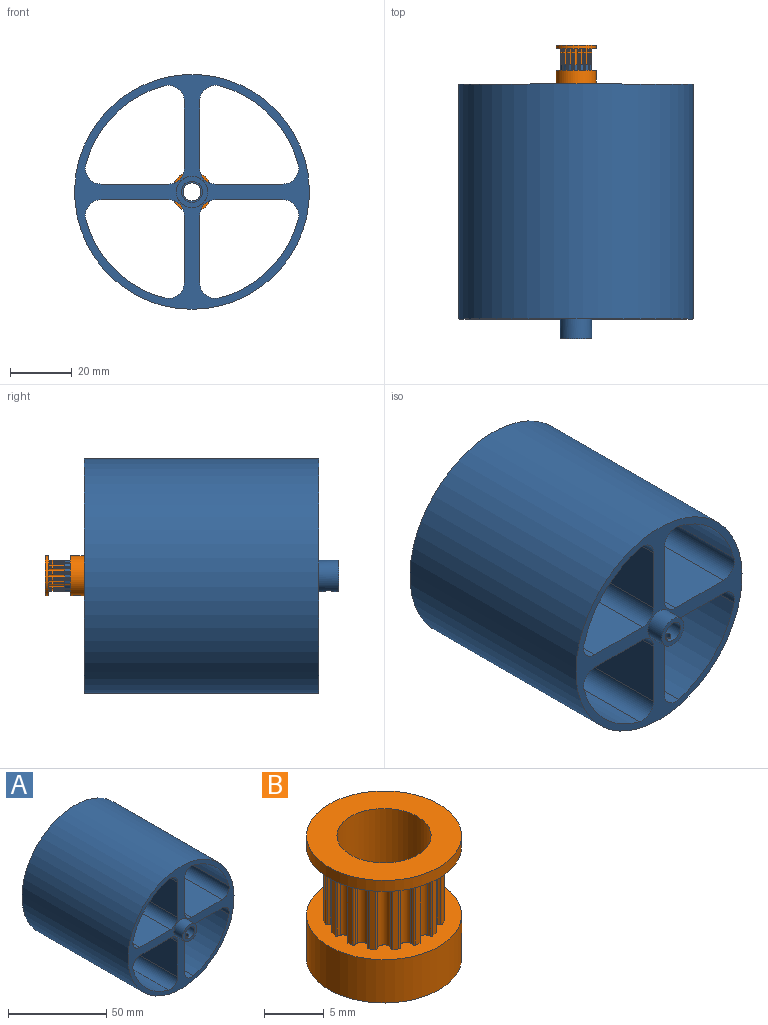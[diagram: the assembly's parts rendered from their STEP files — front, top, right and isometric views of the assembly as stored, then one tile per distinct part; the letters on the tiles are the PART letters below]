
ASSEMBLY  parts=2 mates=1
PART A: 38 faces, bbox 76.2x88.9x76.2 mm
  f0: plane 6.86x6.86mm, normal (0,-1,0), area 10.1mm2, adj f2,f33
  f1: plane 6.86x6.86mm, normal (0,1,0), area 10.1mm2, adj f2,f3
  f2: cylinder r=2.92mm len=76.2mm, axis (0,1,0), area 1398.5mm2, adj f0,f1
  f3: cylinder r=3.43mm len=6.86mm, axis (0,-1,0), area 128.7mm2, adj f1,f4,f37
  f4: plane 10.16x10.16mm, normal (0,1,0), area 44.1mm2, adj f3,f5
  f5: cylinder r=5.08mm len=10.16mm, axis (0,-1,0), area 194.7mm2, adj f4,f32,f37
  f6: cylinder r=5.08mm len=76.2mm, axis (0,1,0), area 705.9mm2, adj f7,f11,f30,f32
  f7: plane 76.2x21.89mm, normal (-1,0,0), area 1668.2mm2, adj f6,f8,f30,f32
  f8: cylinder r=5.08mm len=76.2mm, axis (0,-1,0), area 608mm2, adj f7,f9,f30,f32
  f9: plane 76.2x21.89mm, normal (0,0,1), area 1668.2mm2, adj f8,f10,f30,f32
  f10: cylinder r=5.08mm len=76.2mm, axis (0,1,0), area 705.9mm2, adj f9,f11,f30,f32
  f11: cylinder r=35.56mm len=76.2mm, axis (0,1,0), area 2887mm2, adj f6,f10,f30,f32
  f12: cylinder r=5.08mm len=76.2mm, axis (0,1,0), area 705.9mm2, adj f13,f17,f30,f32
  f13: plane 76.2x21.89mm, normal (1,0,0), area 1668.2mm2, adj f12,f14,f30,f32
  f14: cylinder r=5.08mm len=76.2mm, axis (0,-1,0), area 608mm2, adj f13,f15,f30,f32
  f15: plane 76.2x21.89mm, normal (0,0,-1), area 1668.2mm2, adj f14,f16,f30,f32
  f16: cylinder r=5.08mm len=76.2mm, axis (0,1,0), area 705.9mm2, adj f15,f17,f30,f32
  f17: cylinder r=35.56mm len=76.2mm, axis (0,1,0), area 2887mm2, adj f12,f16,f30,f32
  f18: cylinder r=38.1mm len=76.2mm, axis (0,1,0), area 18241.5mm2, adj f30,f32
  f19: cylinder r=5.08mm len=76.2mm, axis (0,1,0), area 705.9mm2, adj f20,f24,f30,f32
  f20: cylinder r=35.56mm len=76.2mm, axis (0,1,0), area 2887mm2, adj f19,f21,f30,f32
  f21: cylinder r=5.08mm len=76.2mm, axis (0,1,0), area 705.9mm2, adj f20,f22,f30,f32
  f22: plane 76.2x21.89mm, normal (0,0,-1), area 1668.2mm2, adj f21,f23,f30,f32
  f23: cylinder r=5.08mm len=76.2mm, axis (0,-1,0), area 608mm2, adj f22,f24,f30,f32
  f24: plane 76.2x21.89mm, normal (-1,0,0), area 1668.2mm2, adj f19,f23,f30,f32
  f25: cylinder r=5.08mm len=76.2mm, axis (0,1,0), area 705.9mm2, adj f26,f30,f31,f32
  f26: plane 76.2x21.89mm, normal (0,0,1), area 1668.2mm2, adj f25,f27,f30,f32
  f27: cylinder r=5.08mm len=76.2mm, axis (0,-1,0), area 608mm2, adj f26,f28,f30,f32
  f28: plane 76.2x21.89mm, normal (1,0,0), area 1668.2mm2, adj f27,f29,f30,f32
  f29: cylinder r=5.08mm len=76.2mm, axis (0,1,0), area 705.9mm2, adj f28,f30,f31,f32
  f30: plane 76.2x76.2mm, normal (0,-1,0), area 1293.1mm2, adj f6,f7,f8,f9,f10,f11,f12,f13
  f31: cylinder r=35.56mm len=76.2mm, axis (0,1,0), area 2887mm2, adj f25,f29,f30,f32
  f32: plane 76.2x76.2mm, normal (0,1,0), area 1293.1mm2, adj f5,f6,f7,f8,f9,f10,f11,f12
  f33: cylinder r=3.43mm len=6.86mm, axis (0,-1,0), area 128.7mm2, adj f0,f35,f36
  f34: cylinder r=5.08mm len=10.16mm, axis (0,-1,0), area 194.7mm2, adj f30,f35,f36
  f35: plane 10.16x10.16mm, normal (0,-1,0), area 44.1mm2, adj f33,f34
  f36: cylinder r=1.59mm len=3.18mm, axis (0,0,1), area 17.1mm2, adj f33,f34
  f37: cylinder r=1.59mm len=3.18mm, axis (0,0,1), area 17.1mm2, adj f3,f5
PART B: 104 faces, bbox 13x13x12.6 mm
  f0: cylinder r=3.94mm len=12.58mm, axis (0,0,1), area 304.5mm2, adj f2,f102,f103
  f1: cylinder r=6.5mm len=13mm, axis (0,0,1), area 174.4mm2, adj f2,f3,f103
  f2: plane 13x13mm, normal (0,0,-1), area 83.8mm2, adj f0,f1
  f3: plane 13x13mm, normal (0,0,1), area 62.7mm2, adj f1,f4,f5,f6,f7,f8,f9,f10
  f4: cylinder r=0.15mm len=7mm, axis (0,0,-1), area 1.7mm2, adj f3,f5,f99,f100
  f5: cylinder r=1mm len=7mm, axis (0,0,-1), area 1.7mm2, adj f3,f4,f6,f100
  f6: cylinder r=0.56mm len=7mm, axis (0,0,-1), area 9mm2, adj f3,f5,f7,f100
  f7: cylinder r=1mm len=7mm, axis (0,0,-1), area 1.7mm2, adj f3,f6,f8,f100
  f8: cylinder r=0.15mm len=7mm, axis (0,0,-1), area 1.7mm2, adj f3,f7,f9,f100
  f9: plane 7x0.49mm, normal (0.98,0.2,0), area 3.5mm2, adj f3,f8,f10,f100
  f10: cylinder r=0.15mm len=7mm, axis (0,0,-1), area 1.7mm2, adj f3,f9,f11,f100
  f11: cylinder r=1mm len=7mm, axis (0,0,-1), area 1.7mm2, adj f3,f10,f12,f100
  f12: cylinder r=0.56mm len=7mm, axis (0,0,-1), area 9mm2, adj f3,f11,f13,f100
  f13: cylinder r=1mm len=7mm, axis (0,0,-1), area 1.7mm2, adj f3,f12,f14,f100
  f14: cylinder r=0.15mm len=7mm, axis (0,0,-1), area 1.7mm2, adj f3,f13,f15,f100
  f15: plane 7x0.41mm, normal (0.83,0.56,0), area 3.5mm2, adj f3,f14,f16,f100
  f16: cylinder r=0.15mm len=7mm, axis (0,0,-1), area 1.7mm2, adj f3,f15,f17,f100
  f17: cylinder r=1mm len=7mm, axis (0,0,-1), area 1.7mm2, adj f3,f16,f18,f100
  f18: cylinder r=0.56mm len=7mm, axis (0,0,-1), area 9mm2, adj f3,f17,f19,f100
  f19: cylinder r=1mm len=7mm, axis (0,0,-1), area 1.7mm2, adj f3,f18,f20,f100
  f20: cylinder r=0.15mm len=7mm, axis (0,0,-1), area 1.7mm2, adj f3,f19,f21,f100
  f21: plane 7x0.41mm, normal (0.56,0.83,0), area 3.5mm2, adj f3,f20,f22,f100
  f22: cylinder r=0.15mm len=7mm, axis (0,0,-1), area 1.7mm2, adj f3,f21,f23,f100
  f23: cylinder r=1mm len=7mm, axis (0,0,-1), area 1.7mm2, adj f3,f22,f24,f100
  f24: cylinder r=0.56mm len=7mm, axis (0,0,-1), area 9mm2, adj f3,f23,f25,f100
  f25: cylinder r=1mm len=7mm, axis (0,0,-1), area 1.7mm2, adj f3,f24,f26,f100
  f26: cylinder r=0.15mm len=7mm, axis (0,0,-1), area 1.7mm2, adj f3,f25,f27,f100
  f27: plane 7x0.49mm, normal (0.2,0.98,0), area 3.5mm2, adj f3,f26,f28,f100
  f28: cylinder r=0.15mm len=7mm, axis (0,0,-1), area 1.7mm2, adj f3,f27,f29,f100
  f29: cylinder r=1mm len=7mm, axis (0,0,-1), area 1.7mm2, adj f3,f28,f30,f100
  f30: cylinder r=0.56mm len=7mm, axis (0,0,-1), area 9mm2, adj f3,f29,f31,f100
  f31: cylinder r=1mm len=7mm, axis (0,0,-1), area 1.7mm2, adj f3,f30,f32,f100
  f32: cylinder r=0.15mm len=7mm, axis (0,0,-1), area 1.7mm2, adj f3,f31,f33,f100
  f33: plane 7x0.49mm, normal (-0.2,0.98,0), area 3.5mm2, adj f3,f32,f34,f100
  f34: cylinder r=0.15mm len=7mm, axis (0,0,-1), area 1.7mm2, adj f3,f33,f35,f100
  f35: cylinder r=1mm len=7mm, axis (0,0,-1), area 1.7mm2, adj f3,f34,f36,f100
  f36: cylinder r=0.56mm len=7mm, axis (0,0,-1), area 9mm2, adj f3,f35,f37,f100
  f37: cylinder r=1mm len=7mm, axis (0,0,-1), area 1.7mm2, adj f3,f36,f38,f100
  f38: cylinder r=0.15mm len=7mm, axis (0,0,-1), area 1.7mm2, adj f3,f37,f39,f100
  f39: plane 7x0.41mm, normal (-0.56,0.83,0), area 3.5mm2, adj f3,f38,f40,f100
  f40: cylinder r=0.15mm len=7mm, axis (0,0,-1), area 1.7mm2, adj f3,f39,f41,f100
  f41: cylinder r=1mm len=7mm, axis (0,0,-1), area 1.7mm2, adj f3,f40,f42,f100
  f42: cylinder r=0.56mm len=7mm, axis (0,0,-1), area 9mm2, adj f3,f41,f43,f100
  f43: cylinder r=1mm len=7mm, axis (0,0,-1), area 1.7mm2, adj f3,f42,f44,f100
  f44: cylinder r=0.15mm len=7mm, axis (0,0,-1), area 1.7mm2, adj f3,f43,f45,f100
  f45: plane 7x0.41mm, normal (-0.83,0.56,0), area 3.5mm2, adj f3,f44,f46,f100
  f46: cylinder r=0.15mm len=7mm, axis (0,0,-1), area 1.7mm2, adj f3,f45,f47,f100
  f47: cylinder r=1mm len=7mm, axis (0,0,-1), area 1.7mm2, adj f3,f46,f48,f100
  f48: cylinder r=0.56mm len=7mm, axis (0,0,-1), area 9mm2, adj f3,f47,f49,f100
  f49: cylinder r=1mm len=7mm, axis (0,0,-1), area 1.7mm2, adj f3,f48,f50,f100
  f50: cylinder r=0.15mm len=7mm, axis (0,0,-1), area 1.7mm2, adj f3,f49,f51,f100
  f51: plane 7x0.49mm, normal (-0.98,0.2,0), area 3.5mm2, adj f3,f50,f52,f100
  f52: cylinder r=0.15mm len=7mm, axis (0,0,-1), area 1.7mm2, adj f3,f51,f53,f100
  f53: cylinder r=1mm len=7mm, axis (0,0,-1), area 1.7mm2, adj f3,f52,f54,f100
  f54: cylinder r=0.56mm len=7mm, axis (0,0,-1), area 9mm2, adj f3,f53,f55,f100
  f55: cylinder r=1mm len=7mm, axis (0,0,-1), area 1.7mm2, adj f3,f54,f56,f100
  f56: cylinder r=0.15mm len=7mm, axis (0,0,-1), area 1.7mm2, adj f3,f55,f57,f100
  f57: plane 7x0.49mm, normal (-0.98,-0.2,0), area 3.5mm2, adj f3,f56,f58,f100
  f58: cylinder r=0.15mm len=7mm, axis (0,0,-1), area 1.7mm2, adj f3,f57,f59,f100
  f59: cylinder r=1mm len=7mm, axis (0,0,-1), area 1.7mm2, adj f3,f58,f60,f100
  f60: cylinder r=0.56mm len=7mm, axis (0,0,-1), area 9mm2, adj f3,f59,f61,f100
  f61: cylinder r=1mm len=7mm, axis (0,0,-1), area 1.7mm2, adj f3,f60,f62,f100
  f62: cylinder r=0.15mm len=7mm, axis (0,0,-1), area 1.7mm2, adj f3,f61,f63,f100
  f63: plane 7x0.41mm, normal (-0.83,-0.56,0), area 3.5mm2, adj f3,f62,f64,f100
  f64: cylinder r=0.15mm len=7mm, axis (0,0,-1), area 1.7mm2, adj f3,f63,f65,f100
  f65: cylinder r=1mm len=7mm, axis (0,0,-1), area 1.7mm2, adj f3,f64,f66,f100
  f66: cylinder r=0.56mm len=7mm, axis (0,0,-1), area 9mm2, adj f3,f65,f67,f100
  f67: cylinder r=1mm len=7mm, axis (0,0,-1), area 1.7mm2, adj f3,f66,f68,f100
  f68: cylinder r=0.15mm len=7mm, axis (0,0,-1), area 1.7mm2, adj f3,f67,f69,f100
  f69: plane 7x0.41mm, normal (-0.56,-0.83,0), area 3.5mm2, adj f3,f68,f70,f100
  f70: cylinder r=0.15mm len=7mm, axis (0,0,-1), area 1.7mm2, adj f3,f69,f71,f100
  f71: cylinder r=1mm len=7mm, axis (0,0,-1), area 1.7mm2, adj f3,f70,f72,f100
  f72: cylinder r=0.56mm len=7mm, axis (0,0,-1), area 9mm2, adj f3,f71,f73,f100
  f73: cylinder r=1mm len=7mm, axis (0,0,-1), area 1.7mm2, adj f3,f72,f74,f100
  f74: cylinder r=0.15mm len=7mm, axis (0,0,-1), area 1.7mm2, adj f3,f73,f75,f100
  f75: plane 7x0.49mm, normal (-0.2,-0.98,0), area 3.5mm2, adj f3,f74,f76,f100
  f76: cylinder r=0.15mm len=7mm, axis (0,0,-1), area 1.7mm2, adj f3,f75,f77,f100
  f77: cylinder r=1mm len=7mm, axis (0,0,-1), area 1.7mm2, adj f3,f76,f78,f100
  f78: cylinder r=0.56mm len=7mm, axis (0,0,-1), area 9mm2, adj f3,f77,f79,f100
  f79: cylinder r=1mm len=7mm, axis (0,0,-1), area 1.7mm2, adj f3,f78,f80,f100
  f80: cylinder r=0.15mm len=7mm, axis (0,0,-1), area 1.7mm2, adj f3,f79,f81,f100
  f81: plane 7x0.49mm, normal (0.2,-0.98,0), area 3.5mm2, adj f3,f80,f82,f100
  f82: cylinder r=0.15mm len=7mm, axis (0,0,-1), area 1.7mm2, adj f3,f81,f83,f100
  f83: cylinder r=1mm len=7mm, axis (0,0,-1), area 1.7mm2, adj f3,f82,f84,f100
  f84: cylinder r=0.56mm len=7mm, axis (0,0,-1), area 9mm2, adj f3,f83,f85,f100
  f85: cylinder r=1mm len=7mm, axis (0,0,-1), area 1.7mm2, adj f3,f84,f86,f100
  f86: cylinder r=0.15mm len=7mm, axis (0,0,-1), area 1.7mm2, adj f3,f85,f87,f100
  f87: plane 7x0.41mm, normal (0.56,-0.83,0), area 3.5mm2, adj f3,f86,f88,f100
  f88: cylinder r=0.15mm len=7mm, axis (0,0,-1), area 1.7mm2, adj f3,f87,f89,f100
  f89: cylinder r=1mm len=7mm, axis (0,0,-1), area 1.7mm2, adj f3,f88,f90,f100
  f90: cylinder r=0.56mm len=7mm, axis (0,0,-1), area 9mm2, adj f3,f89,f91,f100
  f91: cylinder r=1mm len=7mm, axis (0,0,-1), area 1.7mm2, adj f3,f90,f92,f100
  f92: cylinder r=0.15mm len=7mm, axis (0,0,-1), area 1.7mm2, adj f3,f91,f93,f100
  f93: plane 7x0.41mm, normal (0.83,-0.56,0), area 3.5mm2, adj f3,f92,f94,f100
  f94: cylinder r=0.15mm len=7mm, axis (0,0,-1), area 1.7mm2, adj f3,f93,f95,f100
  f95: cylinder r=1mm len=7mm, axis (0,0,-1), area 1.7mm2, adj f3,f94,f96,f100
  f96: cylinder r=0.56mm len=7mm, axis (0,0,-1), area 9mm2, adj f3,f95,f97,f100
  f97: cylinder r=1mm len=7mm, axis (0,0,-1), area 1.7mm2, adj f3,f96,f98,f100
  f98: cylinder r=0.15mm len=7mm, axis (0,0,-1), area 1.7mm2, adj f3,f97,f99,f100
  f99: plane 7x0.49mm, normal (0.98,-0.2,0), area 3.5mm2, adj f3,f4,f98,f100
  f100: plane 13x13mm, normal (0,0,-1), area 62.7mm2, adj f4,f5,f6,f7,f8,f9,f10,f11
  f101: cylinder r=6.5mm len=13mm, axis (0,0,-1), area 46.1mm2, adj f100,f102
  f102: plane 13x13mm, normal (0,0,1), area 83.8mm2, adj f0,f101
  f103: cylinder r=1.5mm len=3mm, axis (0,-1,0), area 24.6mm2, adj f0,f1
PLACE A t=(-22.52,-46.46,-39.17)mm
PLACE B rot(axis=(-1,0,0),90deg) t=(-22.52,-42.02,-39.17)mm
MATE fastened B.f0 <-> A.f2  axis (0,1,0) through (-22.52,-46.46,-39.17)mm
